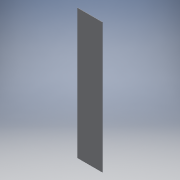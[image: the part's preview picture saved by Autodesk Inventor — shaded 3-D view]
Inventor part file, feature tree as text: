
AUTODESK INVENTOR PART (.ipt)
format: ipt  version: 2016 (Build 200138000, 138)  size: 88,064 bytes
history: native  units: in
note: dims shown in document units (in); Inventor stores cm internally (conversion verified against a paired STEP export)
features: extrude x1, sketch x1
ambient origin geometry x8: Origin, YZ Plane, XZ Plane, XY Plane, X Axis, Y Axis, Z Axis, Center Point
bodies: Solid1 (feature_tree)
feature tree (2):
  extrude  "Extrusion1"  Depth=21.0in
  sketch  "Sketch1"  dims[d0=4.0in d1=21.0in d2=0.0625in d3=0.0in]
